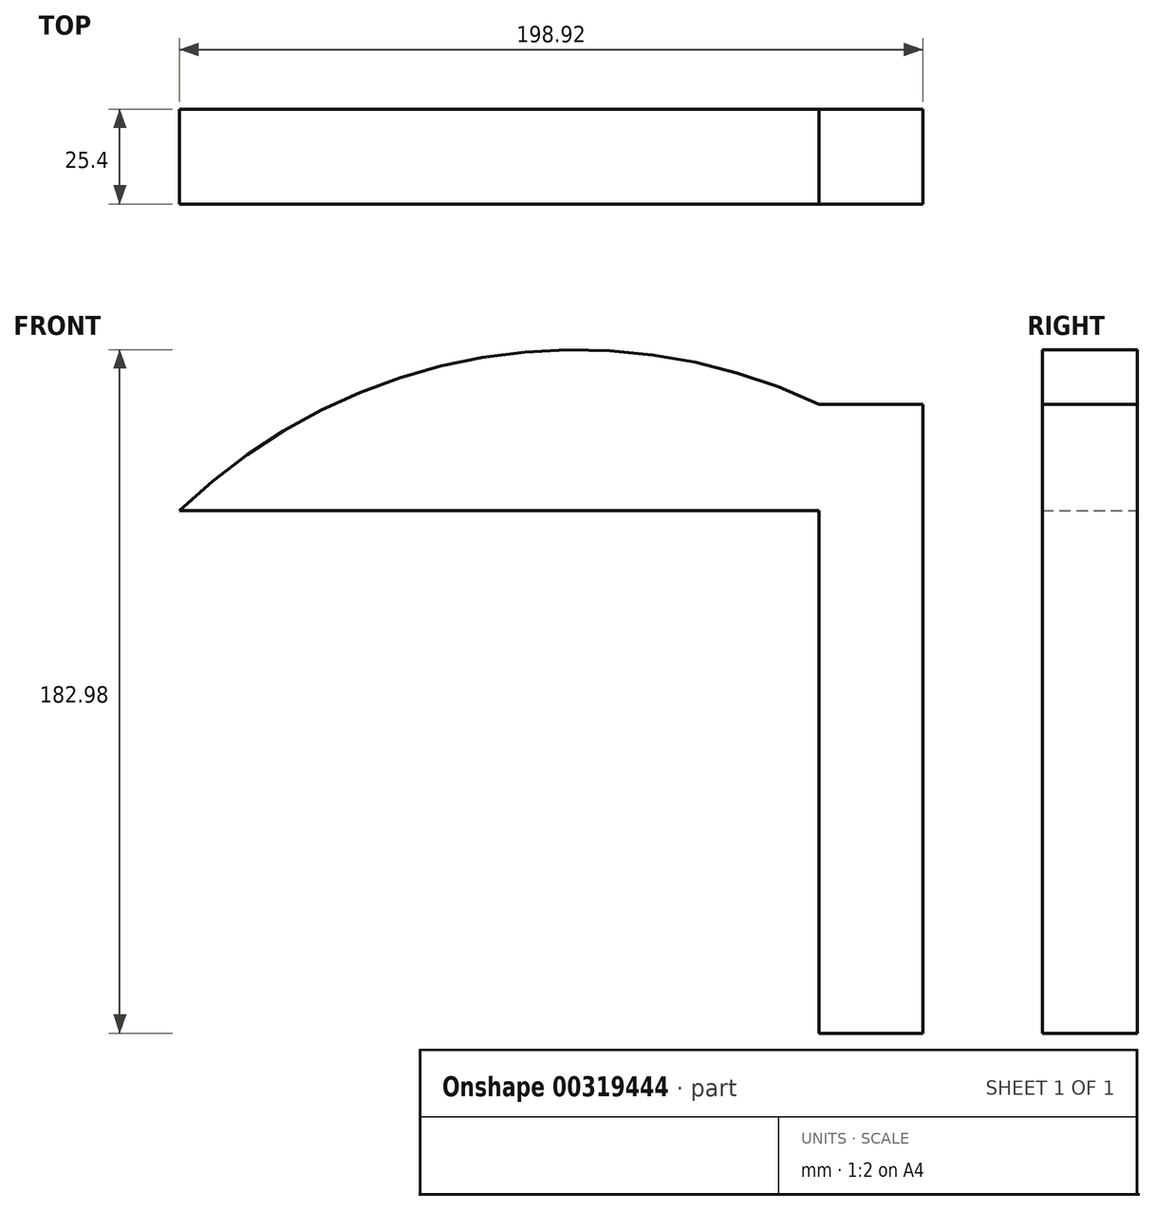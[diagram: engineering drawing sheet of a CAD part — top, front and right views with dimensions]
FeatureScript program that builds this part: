
annotation { "Feature Type Name" : "Feature", "Feature Type Description" : "" }
export const myFeature = defineFeature(function(context is Context, id is Id, definition is map)
    precondition{}
    {
        {
            var Q0;
            Q0=qCreatedBy(makeId("Front.planeOp"),FACE);
            var sketch = newSketch(context, id + "F0", { "sketchPlane" : qUnion([Q0])});
            skLineSegment(sketch, "E0", {"start": v(0, 0) * mm, "end": v(-171.19, 0) * mm});
            skArc(sketch, "E1", {"start": v(0, 28.5) * mm, "mid": v(-90.06, 41.05) * mm, "end": v(-171.19, 0) * mm});
            skLineSegment(sketch, "E2", {"start": v(0, 28.5) * mm, "end": v(27.73, 28.5) * mm});
            skLineSegment(sketch, "E3", {"start": v(27.73, 28.5) * mm, "end": v(27.73, -139.86) * mm});
            skLineSegment(sketch, "E4", {"start": v(27.73, -139.86) * mm, "end": v(0, -139.86) * mm});
            skLineSegment(sketch, "E5", {"start": v(0, -139.86) * mm, "end": v(0, 0) * mm});
            skLineSegment(sketch, "E6", {"start": v(0, 28.5) * mm, "end": v(0, 0) * mm});
            skSolve(sketch);
        }
        {
            var Q0;
            Q0=makeQuery(id+"F0.imprint","IMPRINT",FACE,{"disambiguationData":[TD([[makeQuery(id+"F0.imprint","IMPRINT",EDGE,{"derivedFrom":sQuery(id+"F0.wireOp",EDGE,"E0")}),-1.0]])]});
            var Q1;
            Q1=makeQuery(id+"F0.imprint","IMPRINT",FACE,{"disambiguationData":[TD([[makeQuery(id+"F0.imprint","IMPRINT",EDGE,{"derivedFrom":sQuery(id+"F0.wireOp",EDGE,"E2")}),-1.0]])]});
            extrude(context, id + "F1", {"entities" : qUnion([Q0, Q1]), "endBound" : BoundingType.SYMMETRIC, "depth" : 25.4 * mm});
        }
    });
